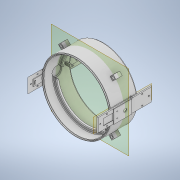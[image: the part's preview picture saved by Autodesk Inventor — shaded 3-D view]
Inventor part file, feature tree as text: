
AUTODESK INVENTOR PART (.ipt)
format: ipt  version: 2020.2 (Build 242310000, 310)  size: 764,928 bytes
history: native  units: mm
features: extrude x26, sketch x26, reference x21, other x8, plane x6, chamfer x2, pattern_circular x2, mirror x1
ambient origin geometry x8: Origin, YZ Plane, XZ Plane, XY Plane, X Axis, Y Axis, Z Axis, Center Point
bodies: Solid1 (feature_tree)
feature tree (92):
  extrude  "Extrusion1"  Depth=205.0mm
  extrude  "Extrusion2"  Depth=208.633333mm
  plane  "Work Plane4"
  extrude  "Extrusion3"  Depth=3.0mm TaperAngle=0.0deg
  extrude  "Extrusion4"  Depth=45.0mm
  extrude  "Extrusion6"  TaperAngle=0.0deg  [1 undecoded]
  extrude  "Extrusion8"  Depth=2.0mm
  chamfer  "Chamfer1"  Distance=20.0mm Angle=360.0deg
  pattern_circular  "Circular Pattern1"  Count=8  [1 undecoded]
  mirror  "Mirror1"
  plane  "Work Plane6"
  plane  "Work Plane8"
  extrude  "Extrusion15"  Depth=20.5mm
  extrude  "Extrusion16"  Depth=1.0mm
  extrude  "Extrusion17"  Depth=4.0mm
  extrude  "Extrusion20"  Depth=20.0mm TaperAngle=0.0deg
  chamfer  "Chamfer2"  Distance=5.0mm
  pattern_circular  "Circular Pattern2"  Count=2 Angle=360.0deg
  extrude  "Extrusion19"  Depth=191.666667mm
  extrude  "Extrusion21"  Depth=3.0mm TaperAngle=0.0deg
  extrude  "Extrusion22"  Depth=20.0mm
  extrude  "Extrusion23"  Depth=0.4mm
  extrude  "Extrusion24"  Depth=6.8mm
  plane  "Work Plane10"
  extrude  "Extrusion25"  TaperAngle=0.0deg  [1 undecoded]
  extrude  "Extrusion26"  TaperAngle=0.0deg  [1 undecoded]
  extrude  "Extrusion27"  TaperAngle=0.0deg  [1 undecoded]
  extrude  "Extrusion28"  Depth=5.0mm
  extrude  "Extrusion29"  Depth=4.0mm TaperAngle=0.0deg
  extrude  "Extrusion30"  Depth=5.0mm TaperAngle=0.0deg
  extrude  "Extrusion34"  Depth=5.0mm TaperAngle=0.0deg
  extrude  "Extrusion35"  Depth=2.0mm
  plane  "Work Plane11"
  extrude  "Extrusion36"  Depth=2.0mm
  extrude  "Extrusion37"  Depth=5.0mm TaperAngle=0.0deg
  extrude  "Extrusion38"  [1 undecoded]
  sketch  "Sketch1"  dims[d0=215.0mm d1=205.0mm]
  sketch  "Sketch2"  dims[d2=40.0mm d3=0.0mm d4=208.633333mm]
  plane  "Work Plane3"
  sketch  "Sketch4"  dims[d5=211.366667mm d6=3.0mm d7=0.0mm]
  sketch  "Sketch5"  dims[d8=45.0mm d9=45.0mm]
  reference  "Reference1"
  sketch  "Sketch6"  dims[d10=3.0mm d11=0.0mm d12=0.0mm]
  sketch  "Sketch8"  dims[d13=2.0mm d14=0.0mm d17=0.1mm]
  reference  "Reference7"
  reference  "Reference8"
  reference  "Reference9"
  reference  "Reference10"
  sketch  "Sketch16"  dims[d18=1.9mm]
  sketch  "Sketch17"  dims[d19=0.0mm d23=20.0mm d24=360.0deg]
  reference  "Reference12"
  reference  "Reference13"
  sketch  "Sketch18"  dims[d26=0.1mm]
  sketch  "Sketch20"  dims[d27=1.0mm d28=0.0mm]
  sketch  "Sketch21"  dims[d29=2.0mm d30=2.0mm d31=45.0deg]
  sketch  "Sketch22"  dims[d67=30.2mm]
  sketch  "Sketch23"  dims[d68=41.0mm d69=80.0mm]
  reference  "Reference14"
  reference  "Reference15"
  sketch  "Sketch24"  dims[d70=40.0mm d71=20.5mm]
  sketch  "Sketch25"  dims[d72=215.0mm d73=0.0mm d74=1.0mm]
  reference  "Reference16"
  reference  "Reference17"
  sketch  "Sketch26"  dims[d75=4.0mm d76=8.0mm]
  reference  "Reference18"
  reference  "Reference19"
  sketch  "Sketch27"  dims[d77=26.0mm d78=20.0mm d79=0.0mm]
  reference  "Reference20"
  reference  "Reference21"
  sketch  "Sketch28"  dims[d80=10.0mm d83=5.0mm d84=0.0mm]
  sketch  "Sketch29"  dims[d85=0.0mm]
  reference  "Reference22"
  reference  "Reference23"
  reference  "Reference24"
  reference  "Reference25"
  sketch  "Sketch30"  dims[d86=2.5mm d87=0.0mm d97=20.0mm d98=360.0deg]
  reference  "Reference26"
  reference  "Reference27"
  sketch  "Sketch31"  dims[d100=215.0mm d101=0.0mm d102=191.666667mm]
  sketch  "Sketch35"  dims[d103=198.333333mm d104=3.0mm d105=0.0mm]
  sketch  "Sketch36"  dims[d106=2.0mm d107=2.0mm d108=45.0deg d110=20.0mm]
  sketch  "Sketch39"  dims[d111=72.5mm d112=0.0mm d114=0.4mm]
  sketch  "Sketch40"  dims[d115=6.0mm d116=6.8mm]
  sketch  "Sketch41"  dims[d117=6.8mm d118=0.0mm d119=0.0mm d120=0.0mm d121=6.0mm d122=4.0mm d123=0.0mm d124=7.5mm d125=0.0mm d126=3.0mm d127=0.0mm d128=2.0mm d129=2.0mm d130=6.0mm d131=0.0mm d132=-7.0mm d133=16.0mm d134=8.0mm d135=0.5mm d136=40.0mm d137=30.2mm d138=3.0mm d139=22.0mm d140=0.0mm d141=2.0mm d142=2.0mm d143=10.0mm d144=0.0mm d145=5.0mm d146=5.0mm d147=4.0mm d148=0.0mm d149=100.0mm d150=0.0mm d151=57.0mm d153=10.0mm d154=1.8mm d155=0.0mm d156=10.0mm d157=0.0mm d158=3.0mm d159=3.0mm d160=5.0mm d161=0.0mm d162=1.5mm d163=0.0mm d176=28.0mm d177=20.0mm d178=6.0mm d179=4.0mm d180=30.0mm d181=1.0mm d182=0.0mm d183=1.0mm d184=0.0mm d185=12.0mm d186=14.0mm d187=4.0mm d188=40.0mm d190=360.0deg d192=20.0mm d193=0.0mm d194=7.0mm d195=40.0mm d197=360.0deg d199=4.0mm d200=0.0mm d201=8.0mm d202=40.0mm d204=360.0deg d206=5.0mm d207=0.0mm d88=0.872665mm]
  other  "<userpath>\OneDrive\Apps\0011_VentControlValve\Assembly.iam"
  other  "Assembly.iam"
  other  "Base:1"
  other  "<userpath>\OneDrive\Apps\0011_VentControlValve\Drawings\Assembly.iam"
  other  "Butterfly Valve:1"
  other  "limitSwitch:2"
  other  "limitSwitch:1"
  other  "motor+Gearbox:1"
note: 6 required parameter values undecoded (feature->parameter linkage not recoverable at this tier; creation-order binding heuristic only, values carry confidence <= 0.55)
